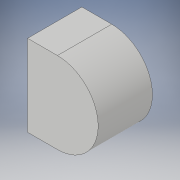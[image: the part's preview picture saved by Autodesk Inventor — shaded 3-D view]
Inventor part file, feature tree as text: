
AUTODESK INVENTOR PART (.ipt)
format: ipt  version: 2019 (Build 230136000, 136)  size: 99,840 bytes
history: native  units: mm
features: other x1, extrude x1, fillet x1, sketch x1
ambient origin geometry x8: Origin, YZ Plane, XZ Plane, XY Plane, X Axis, Y Axis, Z Axis, Center Point
bodies: Body1 (feature_tree)
feature tree (4):
  other  "Bryła1"
  extrude  "Wyciągnięcie proste1"  Depth=1.5mm
  fillet  "Zaokrąglenie1"  Radius=1.3mm
  sketch  "Szkic1"
